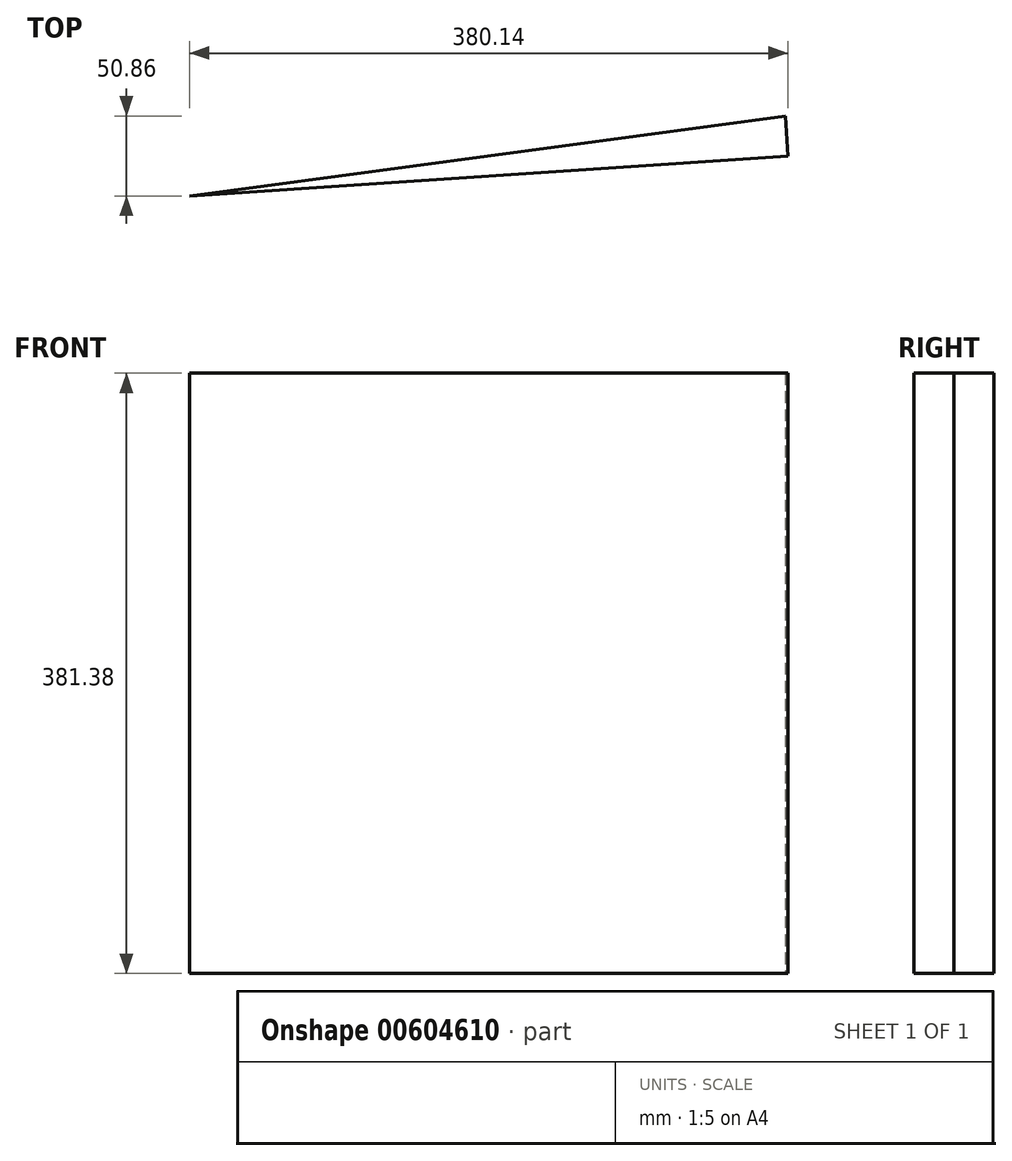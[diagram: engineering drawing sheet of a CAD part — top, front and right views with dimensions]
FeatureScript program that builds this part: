
annotation { "Feature Type Name" : "Feature", "Feature Type Description" : "" }
export const myFeature = defineFeature(function(context is Context, id is Id, definition is map)
    precondition{}
    {
        {
            var Q0;
            Q0=qCreatedBy(makeId("Top.planeOp"),FACE);
            var sketch = newSketch(context, id + "F0", { "sketchPlane" : qUnion([Q0])});
            skLineSegment(sketch, "E0", {"start": v(128.23, -211.11) * mm, "end": v(508.37, -185.6) * mm});
            skLineSegment(sketch, "E1", {"start": v(508.37, -185.6) * mm, "end": v(506.67, -160.25) * mm});
            skLineSegment(sketch, "E2", {"start": v(506.67, -160.25) * mm, "end": v(128.23, -211.11) * mm});
            skSolve(sketch);
        }
        {
            var Q0;
            Q0 = qSketchRegion(id + "F0", true);
            extrude(context, id + "F1", {"entities" : qUnion([Q0]), "depth" : 381.38 * mm, "offsetDistance" : 25.4 * mm});
        }
    });
